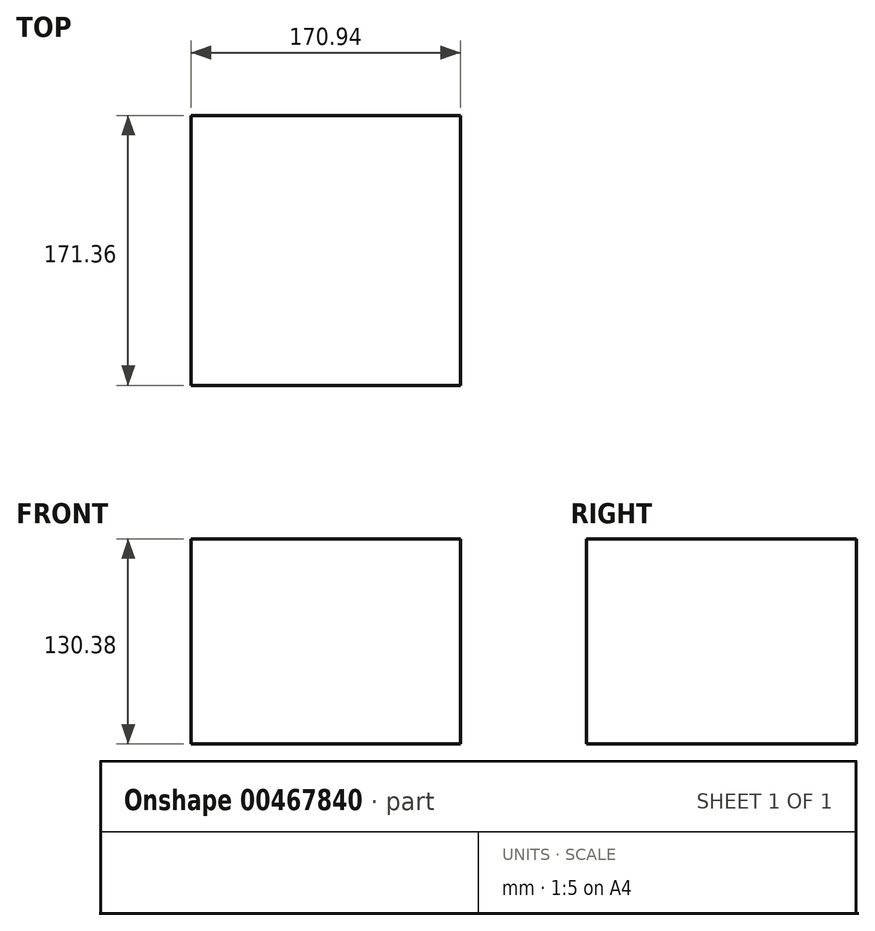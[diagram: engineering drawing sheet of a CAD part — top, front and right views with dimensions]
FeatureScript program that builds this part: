
annotation { "Feature Type Name" : "Feature", "Feature Type Description" : "" }
export const myFeature = defineFeature(function(context is Context, id is Id, definition is map)
    precondition{}
    {
        {
            var Q0;
            Q0=qCreatedBy(makeId("Top.planeOp"),FACE);
            var sketch = newSketch(context, id + "F0", { "sketchPlane" : qUnion([Q0])});
            skLineSegment(sketch, "E0.bottom", {"start": v(85.47, -85.68) * mm, "end": v(-85.47, -85.68) * mm});
            skLineSegment(sketch, "E0.top", {"start": v(85.47, 85.68) * mm, "end": v(-85.47, 85.68) * mm});
            skLineSegment(sketch, "E0.left", {"start": v(85.47, -85.68) * mm, "end": v(85.47, 85.68) * mm});
            skLineSegment(sketch, "E0.right", {"start": v(-85.47, -85.68) * mm, "end": v(-85.47, 85.68) * mm});
            skPoint(sketch, "E0.middle", {"position": v(0, 0) * mm});
            skSolve(sketch);
        }
        {
            var Q0;
            Q0 = qSketchRegion(id + "F0", true);
            extrude(context, id + "F1", {"entities" : qUnion([Q0]), "oppositeDirection" : true, "depth" : 130.38 * mm, "symmetric" : true});
        }
    });
